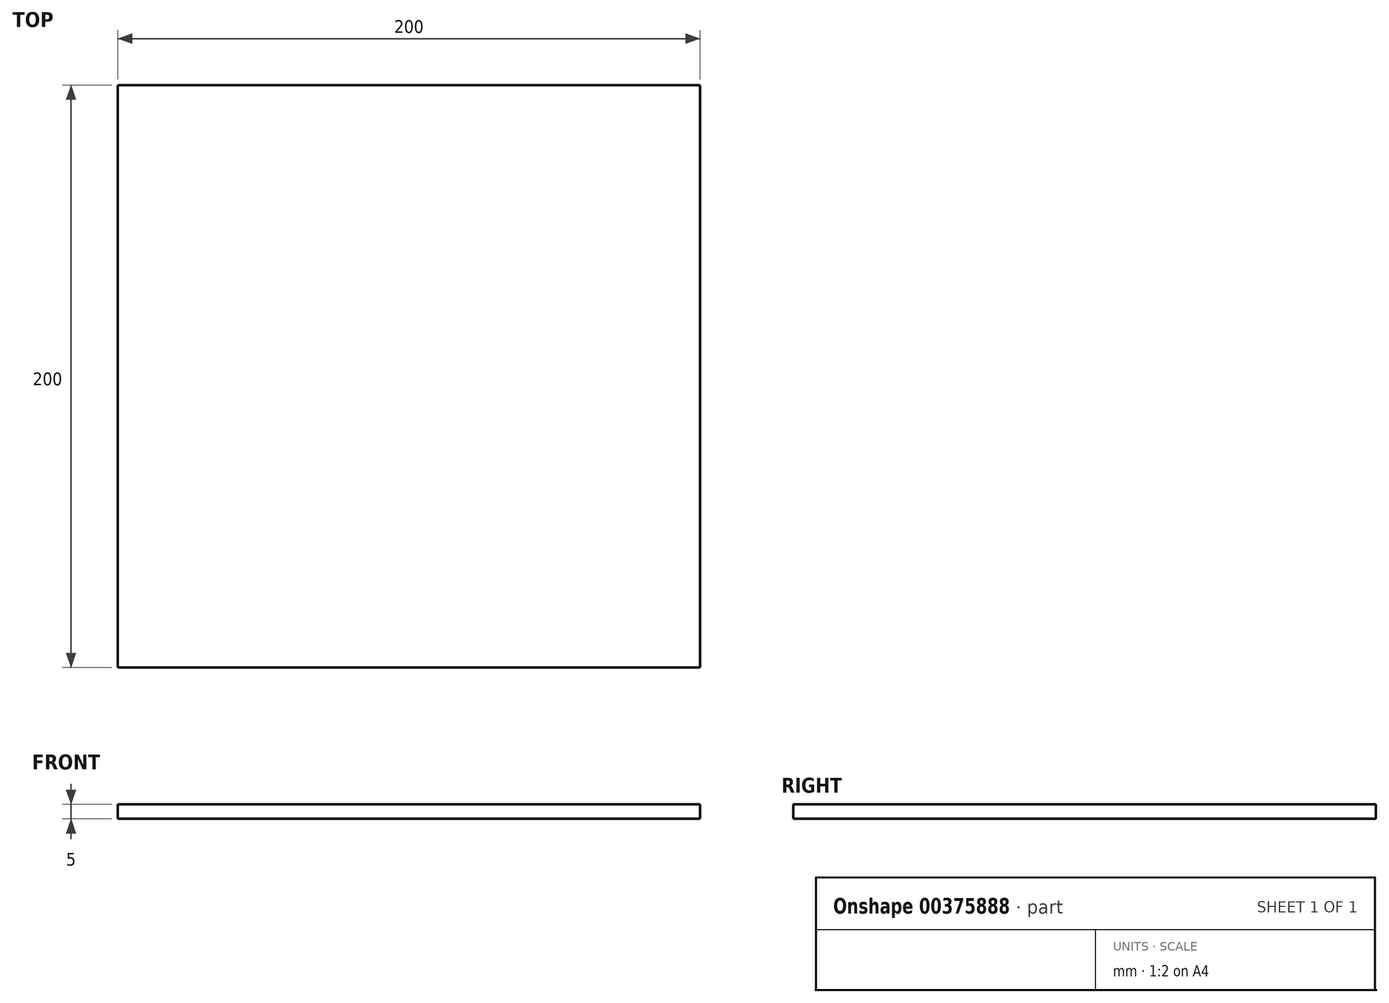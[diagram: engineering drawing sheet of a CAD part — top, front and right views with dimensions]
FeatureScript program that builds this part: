
annotation { "Feature Type Name" : "Feature", "Feature Type Description" : "" }
export const myFeature = defineFeature(function(context is Context, id is Id, definition is map)
    precondition{}
    {
        {
            var Q0;
            Q0=qCreatedBy(makeId("Top.planeOp"),FACE);
            var sketch = newSketch(context, id + "F0", { "sketchPlane" : qUnion([Q0])});
            skLineSegment(sketch, "E0.bottom", {"start": v(100, 100) * mm, "end": v(-100, 100) * mm});
            skLineSegment(sketch, "E0.top", {"start": v(100, -100) * mm, "end": v(-100, -100) * mm});
            skLineSegment(sketch, "E0.left", {"start": v(100, 100) * mm, "end": v(100, -100) * mm});
            skLineSegment(sketch, "E0.right", {"start": v(-100, 100) * mm, "end": v(-100, -100) * mm});
            skPoint(sketch, "E0.middle", {"position": v(0, 0) * mm});
            skSolve(sketch);
        }
        {
            var Q0;
            Q0 = qSketchRegion(id + "F0", true);
            extrude(context, id + "F1", {"entities" : qUnion([Q0]), "depth" : 5 * mm});
        }
    });
